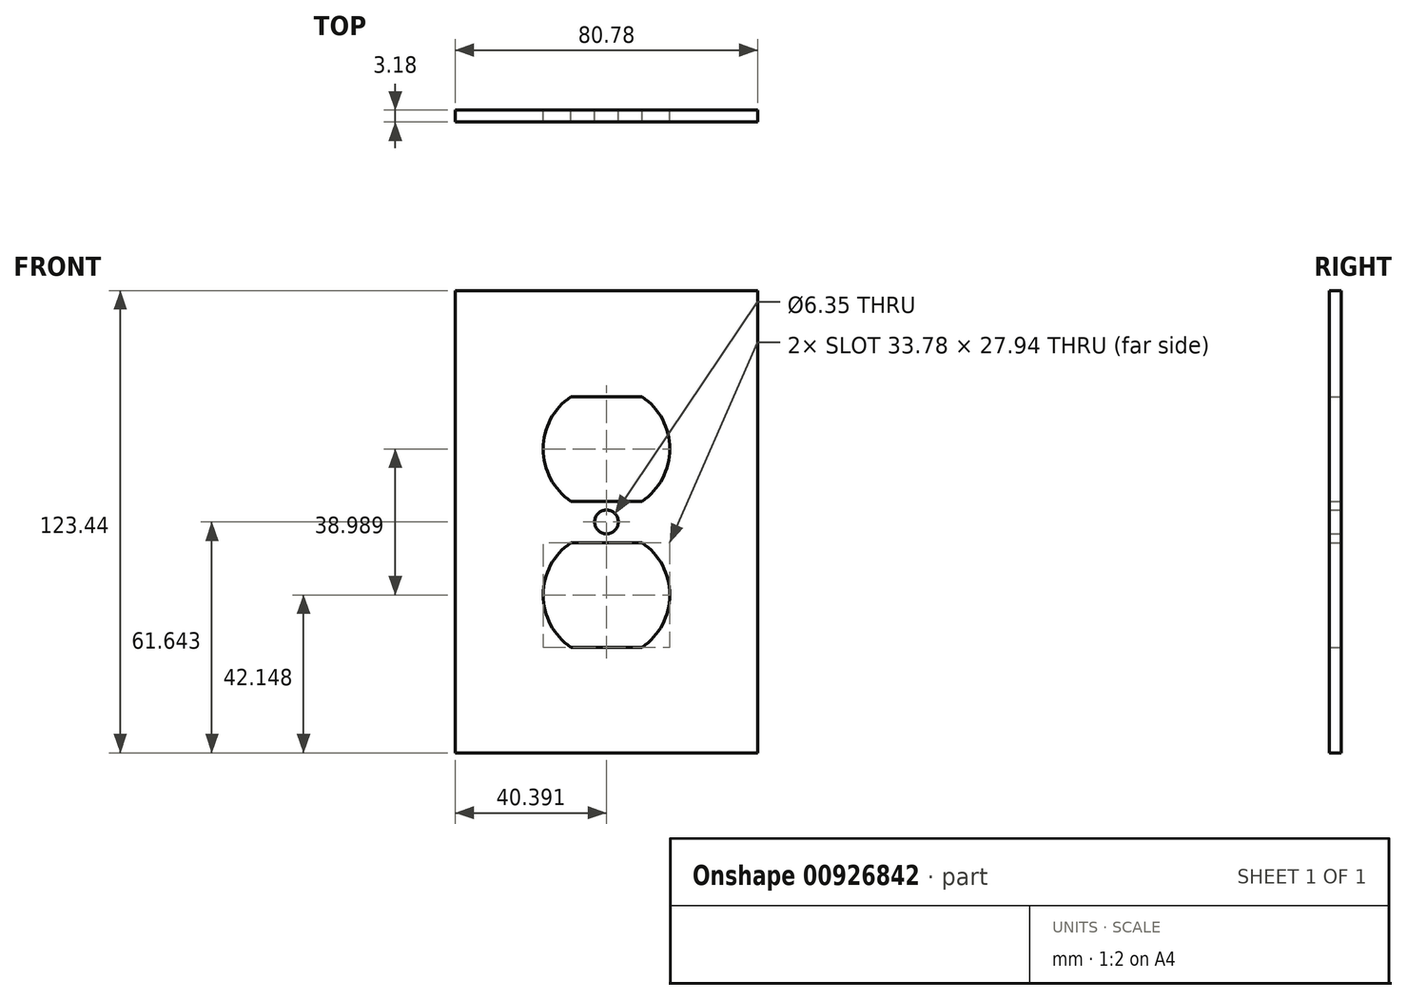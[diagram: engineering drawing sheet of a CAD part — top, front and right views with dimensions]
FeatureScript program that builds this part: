
annotation { "Feature Type Name" : "Feature", "Feature Type Description" : "" }
export const myFeature = defineFeature(function(context is Context, id is Id, definition is map)
    precondition{}
    {
        {
            var Q0;
            Q0=qCreatedBy(makeId("Front.planeOp"),FACE);
            var sketch = newSketch(context, id + "F0", { "sketchPlane" : qUnion([Q0])});
            skArc(sketch, "E0", {"start": v(-9.5, 33.39) * mm, "mid": v(-16.89, 19.42) * mm, "end": v(-9.5, 5.45) * mm});
            skArc(sketch, "E1", {"start": v(9.5, 5.45) * mm, "mid": v(16.9, 19.42) * mm, "end": v(9.5, 33.39) * mm});
            skLineSegment(sketch, "E2", {"start": v(-9.5, 33.39) * mm, "end": v(9.5, 33.39) * mm});
            skLineSegment(sketch, "E3", {"start": v(-9.5, 5.45) * mm, "end": v(9.5, 5.45) * mm});
            skArc(sketch, "E4", {"start": v(-9.5, -5.6) * mm, "mid": v(-16.89, -19.57) * mm, "end": v(-9.5, -33.54) * mm});
            skArc(sketch, "E5", {"start": v(9.5, -33.54) * mm, "mid": v(16.9, -19.57) * mm, "end": v(9.5, -5.6) * mm});
            skLineSegment(sketch, "E6", {"start": v(-9.5, -5.6) * mm, "end": v(9.5, -5.6) * mm});
            skLineSegment(sketch, "E7", {"start": v(-9.5, -33.54) * mm, "end": v(9.5, -33.54) * mm});
            skCircle(sketch, "E8", {"center": v(0, -0.08) * mm, "radius": 3.18 * mm});
            skLineSegment(sketch, "E9.bottom", {"start": v(40.39, 61.72) * mm, "end": v(-40.39, 61.72) * mm});
            skLineSegment(sketch, "E9.top", {"start": v(40.39, -61.72) * mm, "end": v(-40.39, -61.72) * mm});
            skLineSegment(sketch, "E9.left", {"start": v(40.39, 61.72) * mm, "end": v(40.39, -61.72) * mm});
            skLineSegment(sketch, "E9.right", {"start": v(-40.39, 61.72) * mm, "end": v(-40.39, -61.72) * mm});
            skPoint(sketch, "E9.middle", {"position": v(0, 0) * mm});
            skLineSegment(sketch, "E10", {"start": v(0, 19.42) * mm, "end": v(0, -19.57) * mm, "construction": true});
            skLineSegment(sketch, "E11.0", {"start": v(-14.6, 10.93) * mm, "end": v(-14.6, -11.09) * mm, "construction": true});
            skLineSegment(sketch, "E12.0", {"start": v(14.6, 10.93) * mm, "end": v(14.6, -11.09) * mm, "construction": true});
            skSolve(sketch);
        }
        {
            var Q0;
            Q0=makeQuery(id+"F0.imprint","IMPRINT",FACE,{"disambiguationData":[TD([[makeQuery(id+"F0.imprint","IMPRINT",EDGE,{"derivedFrom":sQuery(id+"F0.wireOp",EDGE,"E0")}),-1.0]])]});
            extrude(context, id + "F1", {"entities" : qUnion([Q0]), "depth" : 3.17 * mm, "offsetDistance" : 25.4 * mm});
        }
    });
